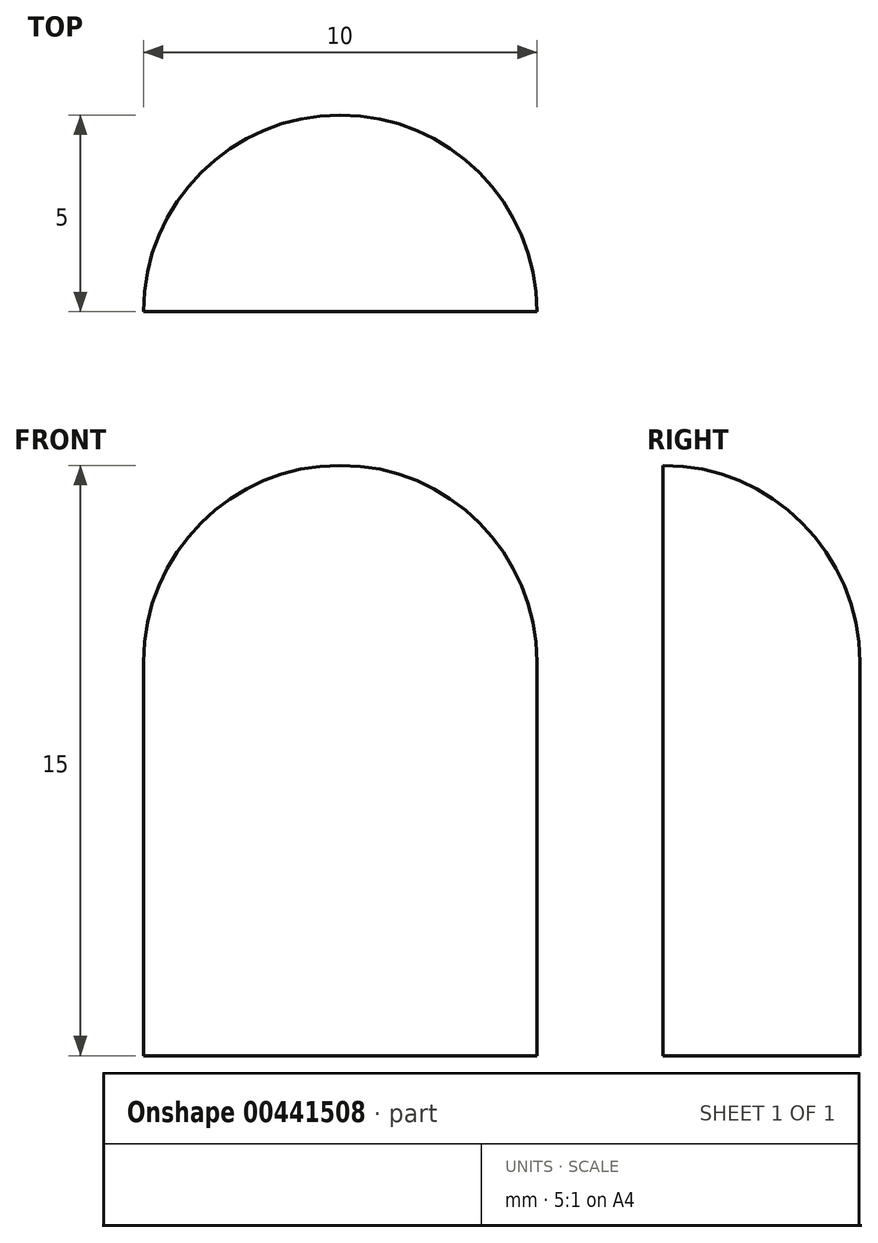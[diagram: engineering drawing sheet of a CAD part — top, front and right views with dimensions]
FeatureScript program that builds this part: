
annotation { "Feature Type Name" : "Feature", "Feature Type Description" : "" }
export const myFeature = defineFeature(function(context is Context, id is Id, definition is map)
    precondition{}
    {
        {
            var Q0;
            Q0=qCreatedBy(makeId("Front.planeOp"),FACE);
            var sketch = newSketch(context, id + "F0", { "sketchPlane" : qUnion([Q0])});
            skArc(sketch, "E0", {"start": v(5, 0) * mm, "mid": v(3.54, 3.54) * mm, "end": v(0, 5) * mm});
            skLineSegment(sketch, "E1", {"start": v(0, -10) * mm, "end": v(5, -10) * mm});
            skLineSegment(sketch, "E2", {"start": v(5, -10) * mm, "end": v(5, 0) * mm});
            skLineSegment(sketch, "E3", {"start": v(0, -10) * mm, "end": v(0, 5) * mm});
            skSolve(sketch);
        }
        {
            var Q0;
            Q0 = qSketchRegion(id + "F0", true);
            var Q1;
            Q1=sQuery(id+"F0.wireOp",EDGE,"E3");
            revolve(context, id + "F1", {"entities" : qUnion([Q0]), "axis" : qUnion([Q1]), "revolveType" : RevolveType.ONE_DIRECTION, "angle" : 180 * degree});
        }
    });
